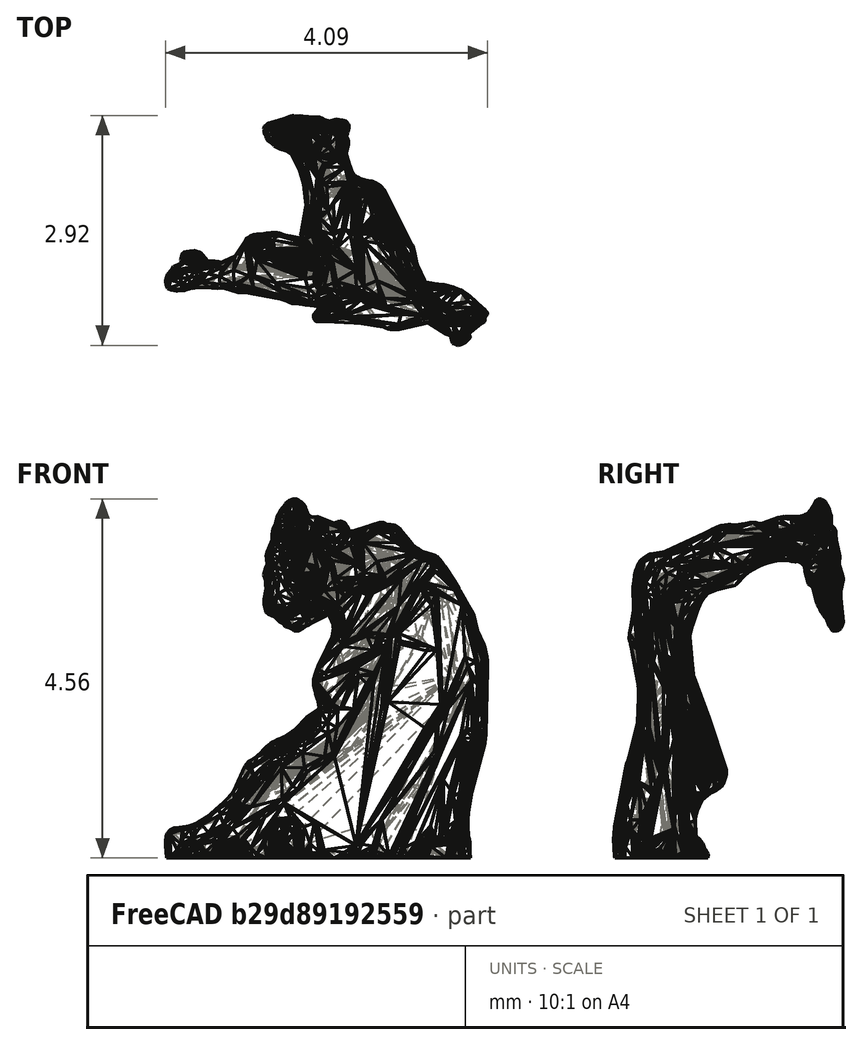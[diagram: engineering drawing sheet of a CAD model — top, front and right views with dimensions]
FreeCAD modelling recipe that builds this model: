
FCSTD DOCUMENT  (FreeCAD 0.20R29603 (Git))
Label: pwp
License: All rights reserved
LicenseURL: http://en.wikipedia.org/wiki/All_rights_reserved
objects: Mesh::Feature×2, Sketcher::SketchObject×2, PartDesign::Line×2, Part::Feature×1, PartDesign::FeatureBase×1, PartDesign::Plane×1, PartDesign::Point×1, PartDesign::Body×1
note: 9 computed .brp shape members not serialized (recipe doc carries the construction recipe); baked Part::Feature solids carry a one-line shape summary decoded from their .brp

FEATURE [Mesh::Feature] pwp
FEATURE [Part::Feature] pwp001
  shape: bbox 4.093 x 2.918 x 4.562 mm, 7946 faces, 0 solids (baked)
FEATURE [Mesh::Feature] ii_sclerite
FEATURE [PartDesign::FeatureBase] BaseFeature
  BaseFeature = -> pwp001
FEATURE [PartDesign::Plane] DatumPlane  label="ii_sclerite_axis1_DatumPlane"
  AttachmentOffset = pos=(0,0,-2.4) rot=(0,0,1;0rad)
  Length = 60
  MapMode = 5
  Placement = pos=(0,2.4,5e-16) rot=(1,0,0;1.5708rad)
  ResizeMode = 0
  Support = -> [XZ_Plane]
  Width = 60
FEATURE [Sketcher::SketchObject] Sketch  label="ii_sclerite_axis1_Sketch"
  FullyConstrained = true
  MapMode = 5
  Placement = pos=(0,2.4,5e-16) rot=(0,0.707107,0.707107;3.14159rad)
  Support = -> [DatumPlane]
  sketch-geometry (5):
    g0: LineSegment StartX=0 StartY=0 StartZ=0 EndX=0 EndY=0.4599 EndZ=0
    g1: LineSegment StartX=0 StartY=0.4599 StartZ=0 EndX=0 EndY=3.0532 EndZ=0
    g2: LineSegment StartX=-4.24024 StartY=5.7028 StartZ=0 EndX=4.24024 EndY=0.403604 EndZ=0
    g3: GeomPoint X=0 Y=3.0532 Z=0
    g4: GeomPoint X=-0.865263 Y=3.59388 Z=0
  constraints (12):
    c: Vertical(g0)
    c: Coincident(g0,g-1)
    c: DistanceY(g0,g0) = 0.4599
    c: Coincident(g1,g0)
    c: Vertical(g1)
    c: DistanceY(g1,g1) = 2.5933
    c: Distance(g2,g2) = 10
    c: Symmetric(g2,g2,g1)
    c: Angle(g2,g-1) = 0.558505
    c: Coincident(g3,g1)
    c: PointOnObject(g4,g2)
    c: Distance(g4,g3) = 1.0203
FEATURE [PartDesign::Line] DatumLine  label="ii_sclerite_axis1_DatumLine"
  AttacherType = Attacher::AttachEngineLine
  Length = 20
  MapMode = 29
  Placement = pos=(-1.3721,2.4,2.19582) rot=(-0.658342,0.658342,0.364925;3.84141rad)
  ResizeMode = 0
  Support = -> [Sketch]
FEATURE [PartDesign::Point] DatumPoint  label="ii_sclerite_axis_DatumPoint"
  AttacherType = Attacher::AttachEnginePoint
  MapMode = 37
  Placement = pos=(0.865263,2.4,3.59388) rot=(0,0,1;0rad)
  Support = -> [Sketch]
FEATURE [Sketcher::SketchObject] Sketch001  label="ii_sclerite_axis2_Sketch"
  ExternalGeometry = -> [DatumPoint,Sketch]
  FullyConstrained = true
  MapMode = 5
  Placement = pos=(0,2.4,5e-16) rot=(0,0.707107,0.707107;3.14159rad)
  Support = -> [DatumPlane]
  sketch-geometry (2):
    g0: LineSegment StartX=-2.88969 StartY=0.354121 StartZ=0 EndX=-0.865263 EndY=3.59388 EndZ=0
    g1: LineSegment StartX=-0.865263 StartY=3.59388 StartZ=0 EndX=1.15916 EndY=6.83363 EndZ=0
  constraints (6):
    c: Coincident(g1,g0)
    c: Equal(g0,g1)
    c: Parallel(g1,g0)
    c: Coincident(g0,g-3)
    c: Perpendicular(g-4,g1)
    c: Distance(g1,g0) = 7.6405
FEATURE [PartDesign::Line] DatumLine001  label="ii_sclerite_axis2_DatumLine"
  AttacherType = Attacher::AttachEngineLine
  Length = 20
  MapMode = 29
  Placement = pos=(2.23736,2.4,1.39806) rot=(0.265728,-0.265728,-0.926703;1.64685rad)
  ResizeMode = 0
  Support = -> [Sketch001]
FEATURE [PartDesign::Body] Body  label="pwp_Body"
  BaseFeature = -> pwp001
  Group = -> [BaseFeature,DatumPlane,Sketch,DatumLine,DatumPoint,Sketch001,DatumLine001]
  Origin = -> Origin
  Tip = -> BaseFeature
